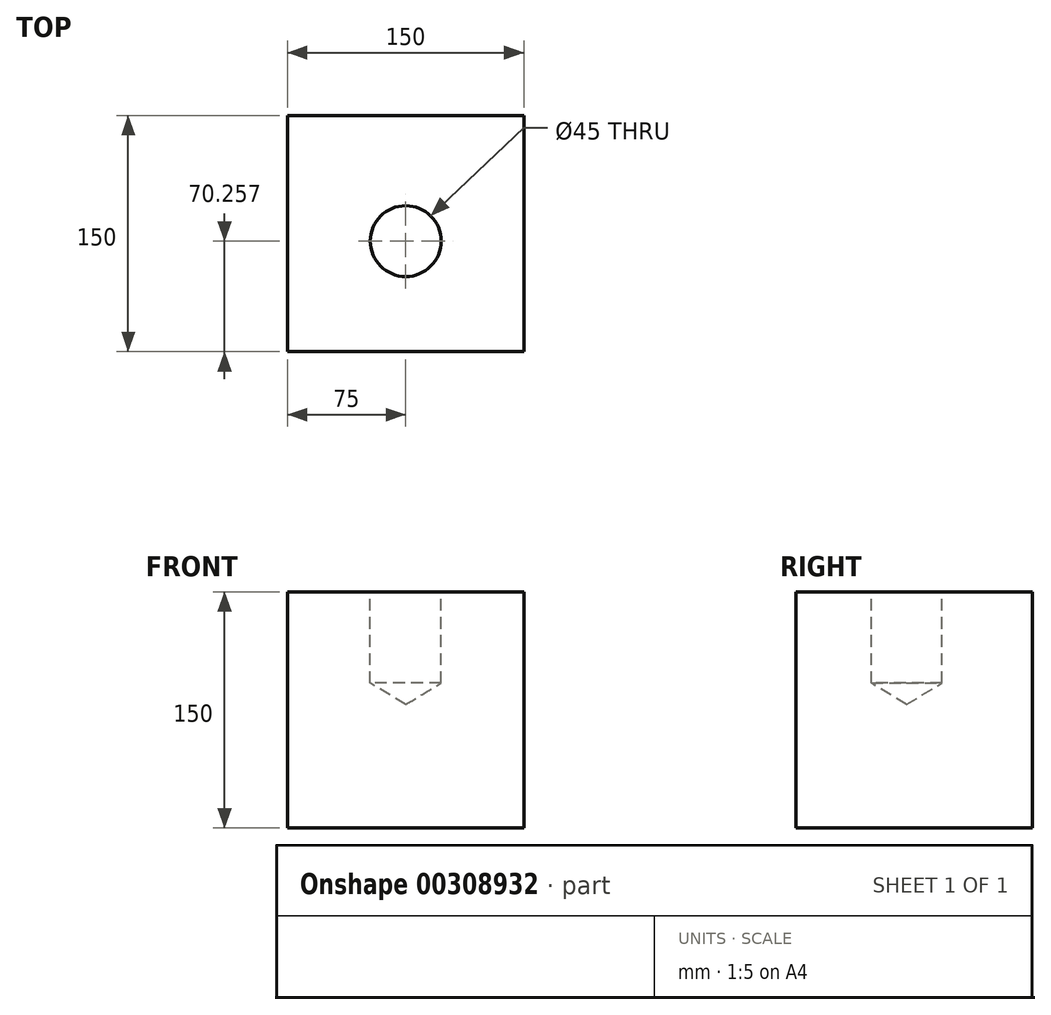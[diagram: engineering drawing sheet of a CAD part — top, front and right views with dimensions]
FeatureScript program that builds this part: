
annotation { "Feature Type Name" : "Feature", "Feature Type Description" : "" }
export const myFeature = defineFeature(function(context is Context, id is Id, definition is map)
    precondition{}
    {
        {
            var Q0;
            Q0=qCreatedBy(makeId("Front.planeOp"),FACE);
            var sketch = newSketch(context, id + "F0", { "sketchPlane" : qUnion([Q0])});
            skLineSegment(sketch, "E0.bottom", {"start": v(-75, 75) * mm, "end": v(75, 75) * mm});
            skLineSegment(sketch, "E0.top", {"start": v(-75, -75) * mm, "end": v(75, -75) * mm});
            skLineSegment(sketch, "E0.left", {"start": v(-75, 75) * mm, "end": v(-75, -75) * mm});
            skLineSegment(sketch, "E0.right", {"start": v(75, 75) * mm, "end": v(75, -75) * mm});
            skPoint(sketch, "E0.middle", {"position": v(0, 0) * mm});
            skSolve(sketch);
        }
        {
            var Q0;
            Q0=makeQuery(id+"F0.imprint","IMPRINT",FACE,{"disambiguationData":[TD([[makeQuery(id+"F0.imprint","IMPRINT",EDGE,{"derivedFrom":sQuery(id+"F0.wireOp",EDGE,"E0.bottom")}),-1.0]])]});
            extrude(context, id + "F1", {"entities" : qUnion([Q0]), "depth" : 150 * mm});
        }
        {
            var Q0;
            Q0=makeQuery(id+"F1.opExtrude","SWEPT_FACE",FACE,{"disambiguationData":[OSD([sQuery(id+"F0.wireOp",EDGE,"E0.bottom")])]});
            var sketch = newSketch(context, id + "F2", { "sketchPlane" : qUnion([Q0])});
            skPoint(sketch, "E1", {"position": v(0, -79.74) * mm});
            skSolve(sketch);
        }
        {
            var Q0;
            Q0=sQuery(id+"F2.wireOp",VERTEX,"E1");
            var Q1;
            Q1=makeQuery(id+"F1.opExtrude","SWEPT_BODY",BODY,{"disambiguationData":[OSD([sQuery(id+"F0.wireOp",EDGE,"E0.bottom"),sQuery(id+"F0.wireOp",EDGE,"E0.top"),sQuery(id+"F0.wireOp",EDGE,"E0.left"),sQuery(id+"F0.wireOp",EDGE,"E0.right")])]});
            hole(context, id + "F3", {"style" : HoleStyle.SIMPLE, "endStyle" : HoleEndStyle.BLIND, "holeDiameter" : 45 * mm, "holeDepth" : 58 * mm, "tappedDepth" : 12 * mm, "tapClearance" : 3, "startFromSketch" : true, "locations" : qUnion([Q0]), "scope" : qUnion([Q1])});
        }
    });
